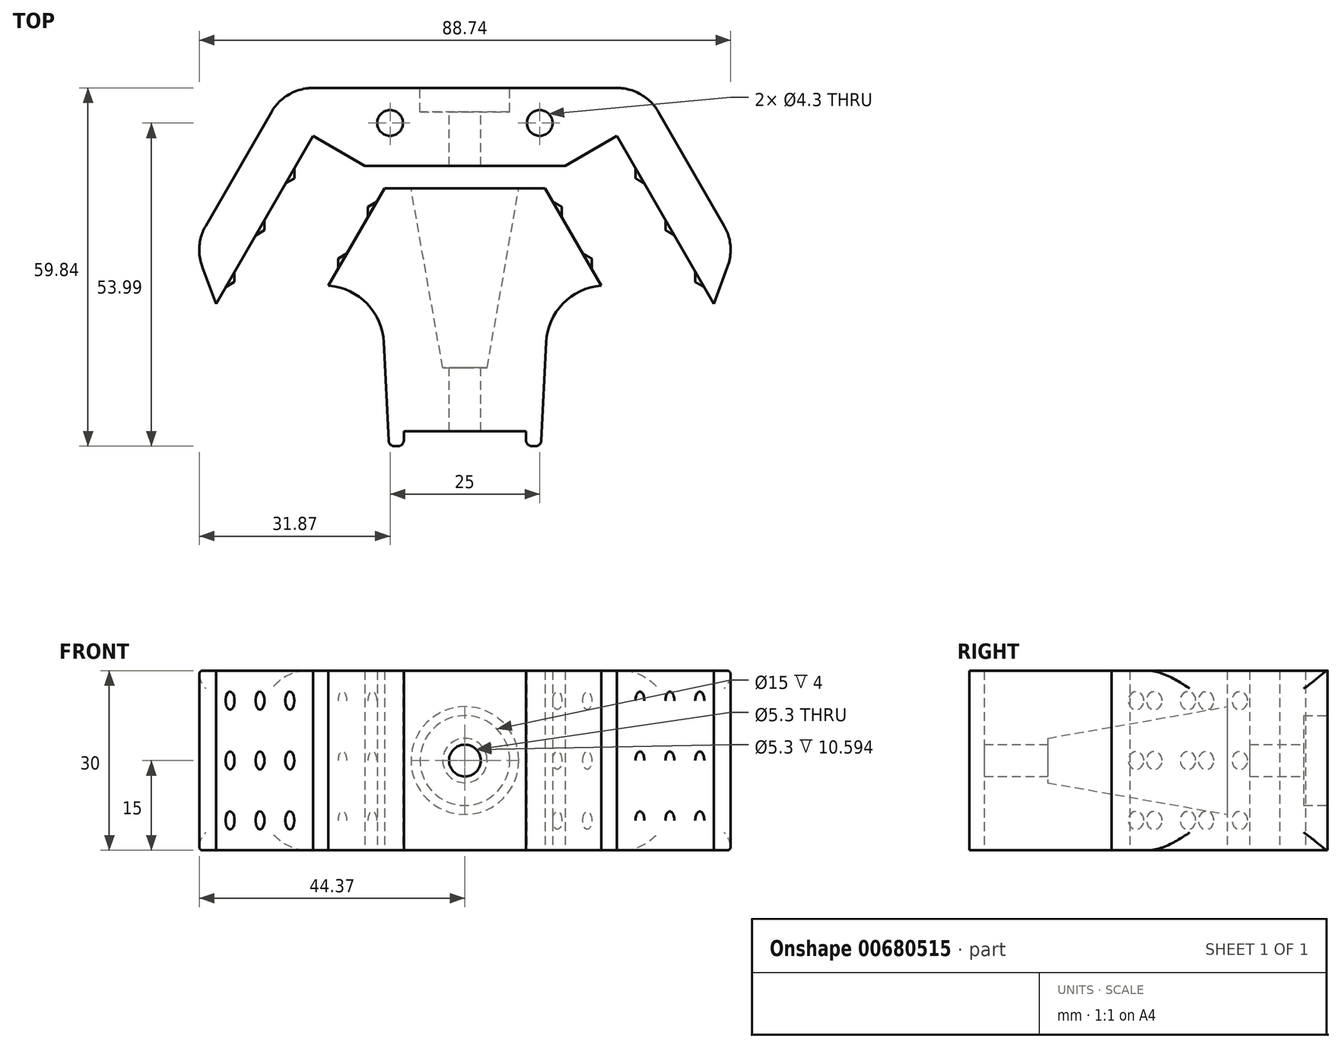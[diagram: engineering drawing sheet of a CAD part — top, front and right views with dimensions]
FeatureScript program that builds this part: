
annotation { "Feature Type Name" : "Feature", "Feature Type Description" : "" }
export const myFeature = defineFeature(function(context is Context, id is Id, definition is map)
    precondition{}
    {
        {
            assignVariable(context, id + "F0", {"name" : "hole_dia", "anyValue" : 5.3});
        }
        {
            var Q0;
            Q0=qCreatedBy(makeId("Top.planeOp"),FACE);
            var sketch = newSketch(context, id + "F1", { "sketchPlane" : qUnion([Q0])});
            skLineSegment(sketch, "E0", {"start": v(-9.8, 0) * mm, "end": v(9.8, 0) * mm, "construction": true});
            skLineSegment(sketch, "E1.bottom", {"start": v(9.8, 0) * mm, "end": v(13.4, -6.25) * mm, "construction": true});
            skLineSegment(sketch, "E1.top", {"start": v(25.38, 9) * mm, "end": v(73.78, -74.83) * mm});
            skLineSegment(sketch, "E1.left", {"start": v(9.8, 0) * mm, "end": v(16.72, 4) * mm, "construction": true});
            skLineSegment(sketch, "E2.bottom", {"start": v(-9.8, 0) * mm, "end": v(-13.4, -6.25) * mm, "construction": true});
            skLineSegment(sketch, "E2.top", {"start": v(-25.38, 9) * mm, "end": v(-76.96, -80.34) * mm});
            skLineSegment(sketch, "E2.left", {"start": v(-9.8, 0) * mm, "end": v(-16.72, 4) * mm, "construction": true});
            skLineSegment(sketch, "E3", {"start": v(0, 0) * mm, "end": v(0, 18.24) * mm, "construction": true});
            skLineSegment(sketch, "E4", {"start": v(-25.38, 9) * mm, "end": v(25.38, 9) * mm, "construction": true});
            skLineSegment(sketch, "E5.0", {"start": v(30, 17) * mm, "end": v(80.7, -70.83) * mm});
            skLineSegment(sketch, "E5.1", {"start": v(-30, 17) * mm, "end": v(30, 17) * mm});
            skLineSegment(sketch, "E5.2", {"start": v(-30, 17) * mm, "end": v(-83.89, -76.34) * mm});
            skPoint(sketch, "E6", {"position": v(-45.17, -9.27) * mm});
            skLineSegment(sketch, "E7", {"start": v(-45.17, -9.27) * mm, "end": v(-41.58, -19.05) * mm});
            skLineSegment(sketch, "E8.MirrorCS", {"start": v(45.17, -9.27) * mm, "end": v(41.58, -19.05) * mm});
            skLineSegment(sketch, "E9.0", {"start": v(-5.17, -8) * mm, "end": v(-54.44, -93.34) * mm});
            skLineSegment(sketch, "E9.1", {"start": v(-5.17, -8) * mm, "end": v(5.17, -8) * mm});
            skLineSegment(sketch, "E9.2", {"start": v(5.17, -8) * mm, "end": v(51.26, -87.83) * mm});
            skLineSegment(sketch, "E10", {"start": v(-22.8, -22.52) * mm, "end": v(-13.97, -23.24) * mm});
            skLineSegment(sketch, "E11.MirrorCS", {"start": v(22.8, -22.52) * mm, "end": v(13.97, -23.24) * mm});
            skLineSegment(sketch, "E12", {"start": v(-16.72, 4) * mm, "end": v(16.72, 4) * mm});
            skLineSegment(sketch, "E13", {"start": v(-13.4, -6.25) * mm, "end": v(13.4, -6.25) * mm});
            skPoint(sketch, "E14.middle", {"position": v(0, 9) * mm});
            skCircle(sketch, "E15", {"center": v(-12.5, 11.15) * mm, "radius": 2.15 * mm});
            skCircle(sketch, "E16.MirrorC", {"center": v(12.5, 11.15) * mm, "radius": 2.15 * mm});
            skLineSegment(sketch, "E17", {"start": v(-16.72, 4) * mm, "end": v(-25.38, 9) * mm});
            skLineSegment(sketch, "E18", {"start": v(-13.4, -6.25) * mm, "end": v(-61.37, -89.34) * mm});
            skLineSegment(sketch, "E19", {"start": v(13.4, -6.25) * mm, "end": v(58.2, -83.83) * mm});
            skLineSegment(sketch, "E20", {"start": v(16.72, 4) * mm, "end": v(25.38, 9) * mm});
            skLineSegment(sketch, "E21", {"start": v(0, 0) * mm, "end": v(0, -46.64) * mm, "construction": true});
            skLineSegment(sketch, "E22", {"start": v(0, -26.83) * mm, "end": v(0, -37.28) * mm, "construction": true});
            skLineSegment(sketch, "E23", {"start": v(0, -37.28) * mm, "end": v(-9.9, -37.28) * mm, "construction": true});
            skLineSegment(sketch, "E24", {"start": v(-9.9, -37.28) * mm, "end": v(-28.77, -37.28) * mm, "construction": true});
            skLineSegment(sketch, "E25", {"start": v(0, -46.64) * mm, "end": v(-36.72, -46.64) * mm, "construction": true});
            skLineSegment(sketch, "E26", {"start": v(-13.97, -23.24) * mm, "end": v(-12.7, -49.34) * mm});
            skLineSegment(sketch, "E27", {"start": v(-12.7, -49.34) * mm, "end": v(-10.2, -49.34) * mm});
            skLineSegment(sketch, "E28", {"start": v(-10.2, -49.34) * mm, "end": v(-10.2, -46.84) * mm});
            skLineSegment(sketch, "E29", {"start": v(-10.2, -46.84) * mm, "end": v(0, -46.84) * mm});
            skLineSegment(sketch, "E30.MirrorCS", {"start": v(13.97, -23.24) * mm, "end": v(12.7, -49.34) * mm});
            skLineSegment(sketch, "E31.MirrorCS", {"start": v(12.7, -49.34) * mm, "end": v(10.2, -49.34) * mm});
            skLineSegment(sketch, "E32.MirrorCS", {"start": v(10.2, -46.84) * mm, "end": v(0, -46.84) * mm});
            skLineSegment(sketch, "E33.MirrorCS", {"start": v(10.2, -49.34) * mm, "end": v(10.2, -46.84) * mm});
            skSolve(sketch);
        }
        {
            var Q0;
            {var subQ9=sQuery(id+"F1.wireOp",EDGE,"E5.1");Q0=makeQuery(id+"F1.imprint","IMPRINT",FACE,{"disambiguationData":[TD([[makeQuery(id+"F1.imprint","IMPRINT",EDGE,{"derivedFrom":subQ9}),-1.0]])]});}
            var Q1;
            {var subQ0=sQuery(id+"F1.wireOp",EDGE,"E10");Q1=makeQuery(id+"F1.imprint","IMPRINT",FACE,{"disambiguationData":[TD([[makeQuery(id+"F1.imprint","IMPRINT",EDGE,{"derivedFrom":subQ0}),1.0]])]});}
            var Q2;
            {var subQ0=sQuery(id+"F1.wireOp",EDGE,"E9.1");Q2=makeQuery(id+"F1.imprint","IMPRINT",FACE,{"disambiguationData":[TD([[makeQuery(id+"F1.imprint","IMPRINT",EDGE,{"derivedFrom":subQ0}),-1.0]])]});}
            var Q3;
            {var subQ5=sQuery(id+"F1.wireOp",EDGE,"J7vzuXij-dSBP-FEbk-L8kl-vO0QfCGw5M7O");Q3=makeQuery(id+"F1.imprint","IMPRINT",FACE,{"disambiguationData":[TD([[makeQuery(id+"F1.imprint","IMPRINT",EDGE,{"derivedFrom":subQ5}),1.0]])]});}
            extrude(context, id + "F2", {"entities" : qUnion([Q0, Q1, Q2, Q3]), "depth" : 30 * mm, "offsetDistance" : 25 * mm});
        }
        {
            var Q0;
            Q0=makeQuery(id+"F2.opExtrude","SWEPT_EDGE",EDGE,{"disambiguationData":[OSD([sQuery(id+"F1.wireOp",EDGE,"E5.2"),sQuery(id+"F1.wireOp",EDGE,"E7")])]});
            var Q1;
            Q1=makeQuery(id+"F2.opExtrude","SWEPT_EDGE",EDGE,{"disambiguationData":[OSD([sQuery(id+"F1.wireOp",EDGE,"E5.1"),sQuery(id+"F1.wireOp",EDGE,"E5.2")])]});
            var Q2;
            Q2=makeQuery(id+"F2.opExtrude","SWEPT_EDGE",EDGE,{"disambiguationData":[OSD([sQuery(id+"F1.wireOp",EDGE,"E5.0"),sQuery(id+"F1.wireOp",EDGE,"E5.1")])]});
            var Q3;
            Q3=makeQuery(id+"F2.opExtrude","SWEPT_EDGE",EDGE,{"disambiguationData":[OSD([sQuery(id+"F1.wireOp",EDGE,"E5.0"),sQuery(id+"F1.wireOp",EDGE,"E8.MirrorCS")])]});
            fillet(context, id + "F3", {"entities" : qUnion([Q0, Q1, Q2, Q3]), "radius" : 8 * mm, "tangentPropagation" : true, "allowEdgeOverflow" : false});
        }
        {
            var Q0;
            Q0=makeQuery(id+"F2.opExtrude","CAP_EDGE",EDGE,{"disambiguationData":[OSD([sQuery(id+"F1.wireOp",EDGE,"E5.0")])],"isStart":false});
            var Q1;
            Q1=makeQuery(id+"F2.opExtrude","CAP_EDGE",EDGE,{"disambiguationData":[OSD([sQuery(id+"F1.wireOp",EDGE,"E5.2")])],"isStart":false});
            var Q2;
            Q2=makeQuery(id+"F2.opExtrude","CAP_EDGE",EDGE,{"disambiguationData":[OSD([sQuery(id+"F1.wireOp",EDGE,"E5.0")])],"isStart":true});
            var Q3;
            Q3=makeQuery(id+"F2.opExtrude","CAP_EDGE",EDGE,{"disambiguationData":[OSD([sQuery(id+"F1.wireOp",EDGE,"E5.2")])],"isStart":true});
            fillet(context, id + "F4", {"entities" : qUnion([Q0, Q1, Q2, Q3]), "radius" : 3 * mm, "allowEdgeOverflow" : false});
        }
        {
            var Q0;
            Q0=makeQuery(id+"F2.opExtrude","SWEPT_EDGE",EDGE,{"disambiguationData":[OSD([sQuery(id+"F1.wireOp",EDGE,"E9.0"),sQuery(id+"F1.wireOp",EDGE,"E10")])]});
            var Q1;
            Q1=makeQuery(id+"F2.opExtrude","SWEPT_EDGE",EDGE,{"disambiguationData":[OSD([sQuery(id+"F1.wireOp",EDGE,"E9.2"),sQuery(id+"F1.wireOp",EDGE,"E11.MirrorCS")])]});
            fillet(context, id + "F5", {"entities" : qUnion([Q0, Q1]), "radius" : 10 * mm, "tangentPropagation" : true, "allowEdgeOverflow" : false});
        }
        {
            var Q0;
            Q0=makeQuery(id+"F2.opExtrude","SWEPT_FACE",FACE,{"disambiguationData":[OSD([sQuery(id+"F1.wireOp",EDGE,"E2.top")])]});
            var sketch = newSketch(context, id + "F6", { "sketchPlane" : qUnion([Q0])});
            skCircle(sketch, "E34", {"center": v(-32.59, 25) * mm, "radius": 1.5 * mm});
            skCircle(sketch, "E35.0.1.0", {"center": v(-32.59, 15) * mm, "radius": 1.5 * mm});
            skCircle(sketch, "E35.0.2.0", {"center": v(-32.59, 5) * mm, "radius": 1.5 * mm});
            skCircle(sketch, "E35.1.0.0", {"center": v(-22.59, 25) * mm, "radius": 1.5 * mm});
            skCircle(sketch, "E35.1.1.0", {"center": v(-22.59, 15) * mm, "radius": 1.5 * mm});
            skCircle(sketch, "E35.1.2.0", {"center": v(-22.59, 5) * mm, "radius": 1.5 * mm});
            skCircle(sketch, "E35.2.0.0", {"center": v(-12.59, 25) * mm, "radius": 1.5 * mm});
            skCircle(sketch, "E35.2.1.0", {"center": v(-12.59, 15) * mm, "radius": 1.5 * mm});
            skCircle(sketch, "E35.2.2.0", {"center": v(-12.59, 5) * mm, "radius": 1.5 * mm});
            skLineSegment(sketch, "E35.direction1", {"start": v(-32.59, 25) * mm, "end": v(-22.59, 25) * mm, "construction": true});
            skLineSegment(sketch, "E35.direction2", {"start": v(-32.59, 25) * mm, "end": v(-32.59, 15) * mm, "construction": true});
            skLineSegment(sketch, "E36", {"start": v(-32.59, 25) * mm, "end": v(-37.29, 25) * mm, "construction": true});
            skLineSegment(sketch, "E37", {"start": v(-32.59, 25) * mm, "end": v(-32.59, 30) * mm, "construction": true});
            skSolve(sketch);
        }
        {
            var Q0;
            Q0=makeQuery(id+"F2.opExtrude","SWEPT_FACE",FACE,{"disambiguationData":[OSD([sQuery(id+"F1.wireOp",EDGE,"E1.top")])]});
            var sketch = newSketch(context, id + "F7", { "sketchPlane" : qUnion([Q0])});
            skCircle(sketch, "E38", {"center": v(12.59, 25) * mm, "radius": 1.5 * mm});
            skCircle(sketch, "E39.0.1.0", {"center": v(12.59, 15) * mm, "radius": 1.5 * mm});
            skCircle(sketch, "E39.0.2.0", {"center": v(12.59, 5) * mm, "radius": 1.5 * mm});
            skCircle(sketch, "E39.1.0.0", {"center": v(22.59, 25) * mm, "radius": 1.5 * mm});
            skCircle(sketch, "E39.1.1.0", {"center": v(22.59, 15) * mm, "radius": 1.5 * mm});
            skCircle(sketch, "E39.1.2.0", {"center": v(22.59, 5) * mm, "radius": 1.5 * mm});
            skCircle(sketch, "E39.2.0.0", {"center": v(32.59, 25) * mm, "radius": 1.5 * mm});
            skCircle(sketch, "E39.2.1.0", {"center": v(32.59, 15) * mm, "radius": 1.5 * mm});
            skCircle(sketch, "E39.2.2.0", {"center": v(32.59, 5) * mm, "radius": 1.5 * mm});
            skLineSegment(sketch, "E39.direction1", {"start": v(12.59, 25) * mm, "end": v(22.59, 25) * mm, "construction": true});
            skLineSegment(sketch, "E39.direction2", {"start": v(12.59, 25) * mm, "end": v(12.59, 15) * mm, "construction": true});
            skLineSegment(sketch, "E40", {"start": v(32.59, 25) * mm, "end": v(37.29, 25) * mm, "construction": true});
            skLineSegment(sketch, "E41", {"start": v(37.29, 25) * mm, "end": v(32.59, 25) * mm, "construction": true});
            skLineSegment(sketch, "E42", {"start": v(32.59, 25) * mm, "end": v(32.59, 30) * mm, "construction": true});
            skSolve(sketch);
        }
        {
            var Q0;
            Q0=makeQuery(id+"F2.opExtrude","SWEPT_FACE",FACE,{"disambiguationData":[OSD([sQuery(id+"F1.wireOp",EDGE,"E18")])]});
            var sketch = newSketch(context, id + "F8", { "sketchPlane" : qUnion([Q0])});
            skCircle(sketch, "E43", {"center": v(16.2, 25) * mm, "radius": 1.5 * mm});
            skCircle(sketch, "E44.0.1.0", {"center": v(16.2, 15) * mm, "radius": 1.5 * mm});
            skCircle(sketch, "E44.0.2.0", {"center": v(16.2, 5) * mm, "radius": 1.5 * mm});
            skCircle(sketch, "E44.1.0.0", {"center": v(26.2, 25) * mm, "radius": 1.5 * mm});
            skCircle(sketch, "E44.1.1.0", {"center": v(26.2, 15) * mm, "radius": 1.5 * mm});
            skCircle(sketch, "E44.1.2.0", {"center": v(26.2, 5) * mm, "radius": 1.5 * mm});
            skLineSegment(sketch, "E44.direction1", {"start": v(16.2, 25) * mm, "end": v(26.2, 25) * mm, "construction": true});
            skLineSegment(sketch, "E44.direction2", {"start": v(16.2, 25) * mm, "end": v(16.2, 15) * mm, "construction": true});
            skLineSegment(sketch, "E45", {"start": v(26.2, 25) * mm, "end": v(26.2, 30) * mm, "construction": true});
            skLineSegment(sketch, "E46", {"start": v(26.2, 25) * mm, "end": v(30.9, 25) * mm, "construction": true});
            skSolve(sketch);
        }
        {
            var Q0;
            Q0=makeQuery(id+"F2.opExtrude","SWEPT_FACE",FACE,{"disambiguationData":[OSD([sQuery(id+"F1.wireOp",EDGE,"E19")])]});
            var sketch = newSketch(context, id + "F9", { "sketchPlane" : qUnion([Q0])});
            skCircle(sketch, "E47", {"center": v(-26.2, 25) * mm, "radius": 1.5 * mm});
            skCircle(sketch, "E48.0.1.0", {"center": v(-26.2, 15) * mm, "radius": 1.5 * mm});
            skCircle(sketch, "E48.0.2.0", {"center": v(-26.2, 5) * mm, "radius": 1.5 * mm});
            skCircle(sketch, "E48.1.0.0", {"center": v(-16.2, 25) * mm, "radius": 1.5 * mm});
            skCircle(sketch, "E48.1.1.0", {"center": v(-16.2, 15) * mm, "radius": 1.5 * mm});
            skCircle(sketch, "E48.1.2.0", {"center": v(-16.2, 5) * mm, "radius": 1.5 * mm});
            skLineSegment(sketch, "E48.direction1", {"start": v(-26.2, 25) * mm, "end": v(-16.2, 25) * mm, "construction": true});
            skLineSegment(sketch, "E48.direction2", {"start": v(-26.2, 25) * mm, "end": v(-26.2, 15) * mm, "construction": true});
            skLineSegment(sketch, "E49", {"start": v(-26.2, 25) * mm, "end": v(-30.9, 25) * mm});
            skLineSegment(sketch, "E50", {"start": v(-30.9, 25) * mm, "end": v(-26.2, 25) * mm, "construction": true});
            skLineSegment(sketch, "E51", {"start": v(-26.2, 25) * mm, "end": v(-26.2, 30) * mm, "construction": true});
            skSolve(sketch);
        }
        {
            var Q0;
            Q0=qSketchRegion(id+"F8",true);
            extrude(context, id + "F10", {"entities" : qUnion([Q0]), "operationType" : NewBodyOperationType.ADD, "depth" : 1 * mm, "offsetDistance" : 25 * mm, "hasDraft" : true, "draftAngle" : 60 * degree, "draftPullDirection" : true});
        }
        {
            var Q0;
            Q0=qSketchRegion(id+"F6",true);
            extrude(context, id + "F11", {"entities" : qUnion([Q0]), "operationType" : NewBodyOperationType.ADD, "depth" : 1 * mm, "offsetDistance" : 25 * mm, "hasDraft" : true, "draftAngle" : 60 * degree, "draftPullDirection" : true});
        }
        {
            var Q0;
            Q0=qSketchRegion(id+"F7",true);
            extrude(context, id + "F12", {"entities" : qUnion([Q0]), "operationType" : NewBodyOperationType.ADD, "depth" : 1 * mm, "offsetDistance" : 25 * mm, "hasDraft" : true, "draftAngle" : 60 * degree, "draftPullDirection" : true});
        }
        {
            var Q0;
            Q0=qSketchRegion(id+"F9",true);
            extrude(context, id + "F13", {"entities" : qUnion([Q0]), "operationType" : NewBodyOperationType.ADD, "depth" : 1 * mm, "offsetDistance" : 25 * mm, "hasDraft" : true, "draftAngle" : 60 * degree, "draftPullDirection" : true});
        }
        {
            var Q0;
            Q0=makeQuery(id+"F2.opExtrude","SWEPT_BODY",BODY,{"disambiguationData":[OSD([sQuery(id+"F1.wireOp",EDGE,"E9.0"),sQuery(id+"F1.wireOp",EDGE,"E9.2"),sQuery(id+"F1.wireOp",EDGE,"E10"),sQuery(id+"F1.wireOp",EDGE,"E11.MirrorCS"),sQuery(id+"F1.wireOp",EDGE,"J7vzuXij-dSBP-FEbk-L8kl-vO0QfCGw5M7O"),sQuery(id+"F1.wireOp",EDGE,"E13"),sQuery(id+"F1.wireOp",EDGE,"E18"),sQuery(id+"F1.wireOp",EDGE,"E19")])]});
            transform(context, id + "F14", {"entities" : qUnion([Q0]), "transformType" : TransformType.TRANSLATION_3D, "dx" : 0 * mm, "dy" : 6.5 * mm, "dz" : 0 * mm, "makeCopy" : false});
        }
        {
            var Q0;
            Q0=makeQuery(id+"F2.opExtrude","SWEPT_FACE",FACE,{"disambiguationData":[OSD([sQuery(id+"F1.wireOp",EDGE,"E13")])]});
            var sketch = newSketch(context, id + "F15", { "sketchPlane" : qUnion([Q0])});
            skLineSegment(sketch, "E52", {"start": v(0, 30) * mm, "end": v(0, 0) * mm, "construction": true});
            skCircle(sketch, "E53", {"center": v(0, 15) * mm, "radius": 9 * mm});
            skSolve(sketch);
        }
        {
            var Q0;
            Q0=makeQuery(id+"F2.opExtrude","SWEPT_FACE",FACE,{"disambiguationData":[OSD([sQuery(id+"F1.wireOp",EDGE,"E5.1")])]});
            var sketch = newSketch(context, id + "F16", { "sketchPlane" : qUnion([Q0])});
            skCircle(sketch, "E54", {"center": v(0, 15) * mm, "radius": 7.5 * mm});
            skLineSegment(sketch, "E55", {"start": v(0, 0) * mm, "end": v(0, 30) * mm, "construction": true});
            skSolve(sketch);
        }
        {
            var Q0;
            Q0=makeQuery(id+"F15.imprint","IMPRINT",FACE,{"disambiguationData":[TD([[makeQuery(id+"F15.imprint","IMPRINT",EDGE,{"derivedFrom":sQuery(id+"F15.wireOp",EDGE,"E53")}),1.0]])]});
            extrude(context, id + "F17", {"entities" : qUnion([Q0]), "operationType" : NewBodyOperationType.REMOVE, "oppositeDirection" : true, "depth" : 30 * mm, "offsetDistance" : 25 * mm, "hasDraft" : true, "draftAngle" : 10 * degree, "draftPullDirection" : true});
        }
        {
            var Q0;
            Q0 = qSketchRegion(id + "F16", true);
            extrude(context, id + "F18", {"entities" : qUnion([Q0]), "operationType" : NewBodyOperationType.REMOVE, "oppositeDirection" : true, "depth" : 4 * mm, "offsetDistance" : 25 * mm});
        }
        {
            var Q0;
            Q0=makeQuery(id+"F2.opExtrude","SWEPT_EDGE",EDGE,{"disambiguationData":[OSD([sQuery(id+"F1.wireOp",EDGE,"E26"),sQuery(id+"F1.wireOp",EDGE,"E27")])]});
            var Q1;
            Q1=makeQuery(id+"F2.opExtrude","SWEPT_EDGE",EDGE,{"disambiguationData":[OSD([sQuery(id+"F1.wireOp",EDGE,"E27"),sQuery(id+"F1.wireOp",EDGE,"E28")])]});
            var Q2;
            Q2=makeQuery(id+"F2.opExtrude","SWEPT_EDGE",EDGE,{"disambiguationData":[OSD([sQuery(id+"F1.wireOp",EDGE,"E31.MirrorCS"),sQuery(id+"F1.wireOp",EDGE,"E33.MirrorCS")])]});
            var Q3;
            Q3=makeQuery(id+"F2.opExtrude","SWEPT_EDGE",EDGE,{"disambiguationData":[OSD([sQuery(id+"F1.wireOp",EDGE,"E30.MirrorCS"),sQuery(id+"F1.wireOp",EDGE,"E31.MirrorCS")])]});
            var Q4;
            Q4=makeQuery(id+"F18.boolean.opBoolean","COPY",EDGE,{"derivedFrom":makeQuery(id+"F18.opExtrude","CAP_EDGE",EDGE,{"disambiguationData":[OSD([sQuery(id+"F16.wireOp",EDGE,"E54")])],"isStart":true})});
            fillet(context, id + "F19", {"entities" : qUnion([Q0, Q1, Q2, Q3, Q4]), "radius" : 1 * mm, "tangentPropagation" : true, "allowEdgeOverflow" : false});
        }
        {
            var Q0;
            Q0=sQuery(id+"F16.wireOp",VERTEX,"E54.center");
            var Q1;
            Q1=makeQuery(id+"F2.opExtrude","SWEPT_BODY",BODY,{"disambiguationData":[OSD([sQuery(id+"F1.wireOp",EDGE,"E1.top"),sQuery(id+"F1.wireOp",EDGE,"E2.top"),sQuery(id+"F1.wireOp",EDGE,"E5.0"),sQuery(id+"F1.wireOp",EDGE,"E5.1"),sQuery(id+"F1.wireOp",EDGE,"E5.2"),sQuery(id+"F1.wireOp",EDGE,"E7"),sQuery(id+"F1.wireOp",EDGE,"E8.MirrorCS"),sQuery(id+"F1.wireOp",EDGE,"E12"),sQuery(id+"F1.wireOp",EDGE,"E14.bottom"),sQuery(id+"F1.wireOp",EDGE,"E14.top"),sQuery(id+"F1.wireOp",EDGE,"E14.left"),sQuery(id+"F1.wireOp",EDGE,"E14.right"),sQuery(id+"F1.wireOp",EDGE,"E15"),sQuery(id+"F1.wireOp",EDGE,"E16.MirrorC"),sQuery(id+"F1.wireOp",EDGE,"E17"),sQuery(id+"F1.wireOp",EDGE,"E20")])]});
            var Q2;
            Q2=makeQuery(id+"F2.opExtrude","SWEPT_BODY",BODY,{"disambiguationData":[OSD([sQuery(id+"F1.wireOp",EDGE,"E9.0"),sQuery(id+"F1.wireOp",EDGE,"E9.2"),sQuery(id+"F1.wireOp",EDGE,"E10"),sQuery(id+"F1.wireOp",EDGE,"E11.MirrorCS"),sQuery(id+"F1.wireOp",EDGE,"J7vzuXij-dSBP-FEbk-L8kl-vO0QfCGw5M7O"),sQuery(id+"F1.wireOp",EDGE,"E13"),sQuery(id+"F1.wireOp",EDGE,"E18"),sQuery(id+"F1.wireOp",EDGE,"E19")])]});
            hole(context, id + "F20", {"style" : HoleStyle.SIMPLE, "endStyle" : HoleEndStyle.THROUGH, "holeDiameter" : (getVariable(context, 'hole_dia')) * mm, "majorDiameter" : 5 * mm, "isTappedThrough" : true, "tappedDepth" : 12 * mm, "tapClearance" : 3, "startFromSketch" : true, "locations" : qUnion([Q0]), "scope" : qUnion([Q1, Q2])});
        }
    });
